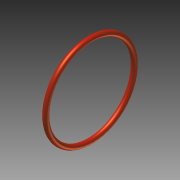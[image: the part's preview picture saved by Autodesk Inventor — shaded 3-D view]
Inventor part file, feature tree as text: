
AUTODESK INVENTOR PART (.ipt)
format: ipt  version: 2012 SP1 (Build 160190100, 190)  size: 124,416 bytes
history: native  units: in
note: dims shown in document units (in); Inventor stores cm internally (conversion verified against a paired STEP export)
features: sketch x2, sweep x1
ambient origin geometry x8: Origin, YZ Plane, XZ Plane, XY Plane, X Axis, Y Axis, Z Axis, Center Point
bodies: Solid1 (feature_tree)
feature tree (3):
  sweep  "Sweep1"
  sketch  "Sketch1"  dims[d0=0.103in d1=1.737in]
  sketch  "Sketch2"  dims[d2=1.943in d3=0.0in]
